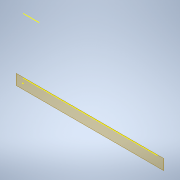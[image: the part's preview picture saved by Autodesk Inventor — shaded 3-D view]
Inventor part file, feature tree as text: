
AUTODESK INVENTOR PART (.ipt)
format: ipt  version: 2021 (Build 250183000, 183)  size: 86,016 bytes
history: native  units: in
note: dims shown in document units (in); Inventor stores cm internally (conversion verified against a paired STEP export)
features: other x4, reference x3, plane x2, sketch x1
ambient origin geometry x8: Origin, YZ Plane, XZ Plane, XY Plane, X Axis, Y Axis, Z Axis, Center Point
feature tree (10):
  plane  "Work Plane1"
  plane  "Work Plane2"
  sketch  "Sketch2"
  reference  "Reference5"
  reference  "Reference6"
  reference  "Reference7"
  parser-record x1  (decoder bookkeeping rows leaked as tree rows — omitted from the tree; the rows remain in map.json)
  other  "fileSocketHanger.iam"
  other  "plateForFileSet:1"
  other  "threeStartConfigurationV01:1"
note: 1 file-system path scrubbed to <path> (originals preserved in map.json)
